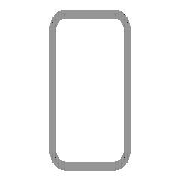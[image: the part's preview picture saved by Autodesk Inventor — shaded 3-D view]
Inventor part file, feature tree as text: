
AUTODESK INVENTOR PART (.ipt)
format: ipt  version: 2025.3 (Build 293356000, 356)  size: 133,632 bytes
history: native  units: mm (DEFAULTED — no unit token found)
features: other x4, sketch x1, plane x1
ambient origin geometry x8: Origin, YZ Plane, XZ Plane, XY Plane, X Axis, Y Axis, Z Axis, Center Point
bodies: Solid1 (feature_tree), Body (feature_tree)
feature tree (6):
  parser-record x1  (decoder bookkeeping rows leaked as tree rows — omitted from the tree; the rows remain in map.json)
  other  "Driven Length"
  other  "Start Plane"
  other  "End Plane"
  sketch  "Sketch3"  dims[d3=575.0mm d4=0.0mm d7=6.0mm d9=40.0mm d11=80.0mm d12=3.0mm d13=30.0mm d14=605.0mm d15=20.0mm d16=40.0mm d17=90.0deg d18=575.0mm]
  plane  "Work Plane3"
